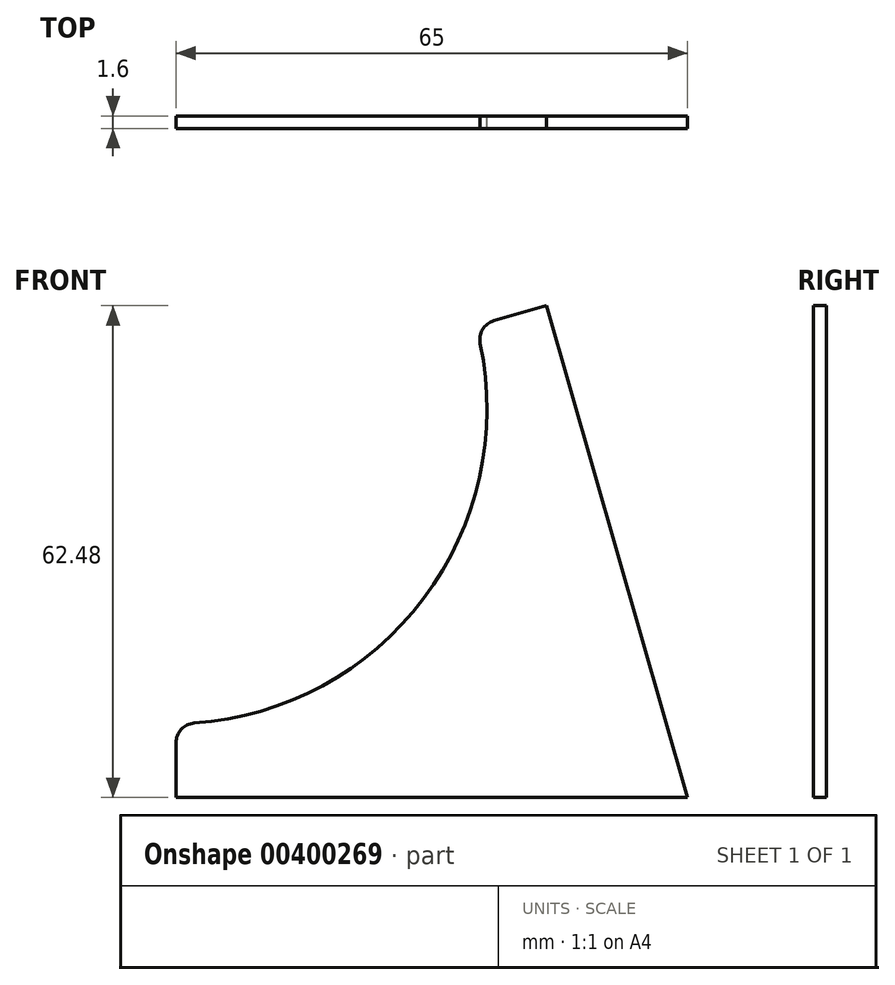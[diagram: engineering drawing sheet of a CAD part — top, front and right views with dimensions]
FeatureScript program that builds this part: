
annotation { "Feature Type Name" : "Feature", "Feature Type Description" : "" }
export const myFeature = defineFeature(function(context is Context, id is Id, definition is map)
    precondition{}
    {
        {
            var Q0;
            Q0=qCreatedBy(makeId("Front.planeOp"),FACE);
            var sketch = newSketch(context, id + "F0", { "sketchPlane" : qUnion([Q0])});
            skLineSegment(sketch, "E0", {"start": v(0, 0) * mm, "end": v(-65, 0) * mm});
            skLineSegment(sketch, "E1", {"start": v(0, 0) * mm, "end": v(-17.92, 62.48) * mm});
            skLineSegment(sketch, "E2", {"start": v(0, 0) * mm, "end": v(-98.55, 74.26) * mm, "construction": true});
            skArc(sketch, "E3", {"start": v(-65, 9.35) * mm, "mid": v(-33.54, 25.28) * mm, "end": v(-26.9, 59.9) * mm});
            skLineSegment(sketch, "E4", {"start": v(-65, 0) * mm, "end": v(-65, 9.35) * mm});
            skLineSegment(sketch, "E5", {"start": v(-17.92, 62.48) * mm, "end": v(-26.9, 59.9) * mm});
            skSolve(sketch);
        }
        {
            var Q0;
            {var subQ0=sQuery(id+"F0.wireOp",EDGE,"E1");Q0=makeQuery(id+"F0.imprint","IMPRINT",FACE,{"disambiguationData":[TD([[makeQuery(id+"F0.imprint","IMPRINT",EDGE,{"derivedFrom":subQ0}),1.0]])]});}
            var Q1;
            {var subQ0=sQuery(id+"F0.wireOp",EDGE,"E0");Q1=makeQuery(id+"F0.imprint","IMPRINT",FACE,{"disambiguationData":[TD([[makeQuery(id+"F0.imprint","IMPRINT",EDGE,{"derivedFrom":subQ0}),-1.0]])]});}
            extrude(context, id + "F1", {"entities" : qUnion([Q0, Q1]), "depth" : 1.6 * mm, "offsetDistance" : 25 * mm});
        }
        {
            var Q0;
            Q0=makeQuery(id+"F1.opExtrude","SWEPT_EDGE",EDGE,{"disambiguationData":[OSD([sQuery(id+"F0.wireOp",EDGE,"E3"),sQuery(id+"F0.wireOp",EDGE,"qbaPFdbs-em9A-A0PR-fsm6-XgC7X7yTzwVX")])]});
            var Q1;
            Q1=makeQuery(id+"F1.opExtrude","SWEPT_EDGE",EDGE,{"disambiguationData":[OSD([sQuery(id+"F0.wireOp",EDGE,"E3"),sQuery(id+"F0.wireOp",EDGE,"upUZ2Jz2-JCQt-sG3k-340y-EpEMQNRWlJYu")])]});
            fillet(context, id + "F2", {"entities" : qUnion([Q0, Q1]), "radius" : 2.5 * mm, "tangentPropagation" : true, "allowEdgeOverflow" : false});
        }
    });
